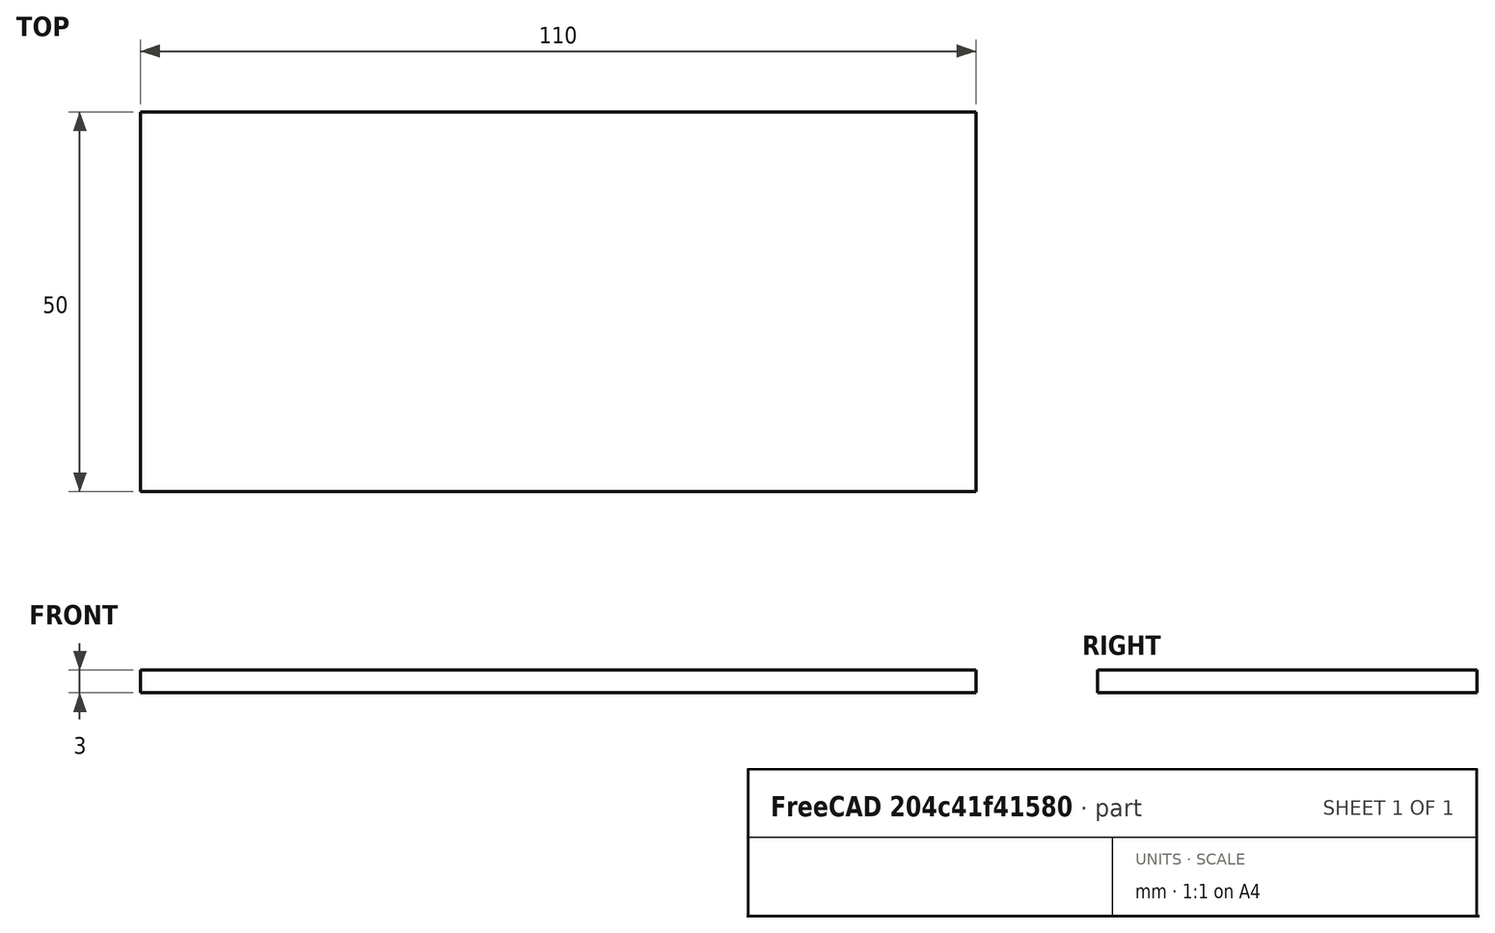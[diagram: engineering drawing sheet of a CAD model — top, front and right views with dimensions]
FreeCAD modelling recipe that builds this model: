
FCSTD DOCUMENT  (FreeCAD 0.17R13528 (Git))
Label: deckel
License: All rights reserved
LicenseURL: http://en.wikipedia.org/wiki/All_rights_reserved
objects: Sketcher::SketchObject×1, PartDesign::Pad×1, PartDesign::Body×1
note: 4 computed .brp shape members not serialized (recipe doc carries the construction recipe); baked Part::Feature solids carry a one-line shape summary decoded from their .brp

FEATURE [Sketcher::SketchObject] Sketch
  MapMode = 5
  Support = -> [XY_Plane]
  sketch-geometry (4):
    g0: LineSegment StartX=-55 StartY=25 StartZ=0 EndX=55 EndY=25 EndZ=0
    g1: LineSegment StartX=55 StartY=25 StartZ=0 EndX=55 EndY=-25 EndZ=0
    g2: LineSegment StartX=55 StartY=-25 StartZ=0 EndX=-55 EndY=-25 EndZ=0
    g3: LineSegment StartX=-55 StartY=-25 StartZ=0 EndX=-55 EndY=25 EndZ=0
  constraints (12):
    c: Coincident(g0,g1)
    c: Coincident(g1,g2)
    c: Coincident(g2,g3)
    c: Coincident(g3,g0)
    c: Horizontal(g0)
    c: Horizontal(g2)
    c: Vertical(g1)
    c: Vertical(g3)
    c: Symmetric(g0,g0,g-2)
    c: Symmetric(g0,g2,g-1)
    c: DistanceX(g0,g0) = 110
    c: DistanceY(g1,g1) = 50
FEATURE [PartDesign::Pad] Pad
  Length = 3
  Length2 = 100
  Profile = -> Sketch
  Type = 0
FEATURE [PartDesign::Body] Body
  Group = -> [Sketch,Pad]
  Origin = -> Origin
  Tip = -> Pad
